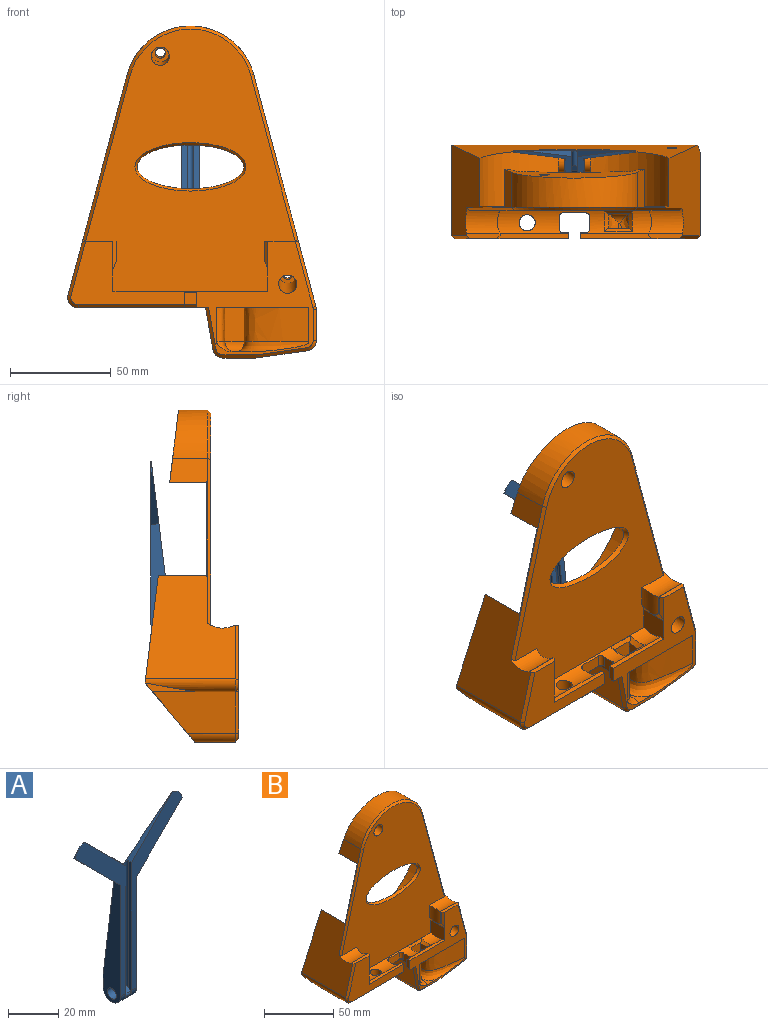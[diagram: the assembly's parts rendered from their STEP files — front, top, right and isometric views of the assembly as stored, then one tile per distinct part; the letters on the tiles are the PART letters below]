
ASSEMBLY  parts=2 mates=1
PART A: 19 faces, bbox 60.4x10x90.5 mm
  f0: plane 85.53x28.64mm, normal (0,-1,0), area 447.3mm2, adj f1,f6,f7,f8,f12,f16
  f1: plane 24.68x24.68mm, normal (0.71,0,0.71), area 51.3mm2, adj f0,f2,f8,f13,f14,f16
  f2: plane 24.68x24.68mm, normal (-0.71,0,0.71), area 51.3mm2, adj f1,f3,f10,f13,f14,f15
  f3: cylinder r=7.37mm len=5.52mm, axis (0,-1,0), area 3.3mm2, adj f2,f4,f10,f13
  f4: plane 25.69x25.69mm, normal (0.71,0,-0.71), area 86.6mm2, adj f3,f5,f10,f13
  f5: plane 59.32x10mm, normal (1,0,0), area 414.2mm2, adj f4,f9,f10,f11,f12,f13
  f6: plane 59.32x10mm, normal (-1,0,0), area 414.2mm2, adj f0,f7,f9,f11,f12,f13
  f7: plane 25.69x25.69mm, normal (-0.71,0,-0.71), area 86.6mm2, adj f0,f6,f8,f13
  f8: cylinder r=7.37mm len=5.52mm, axis (0,-1,0), area 3.3mm2, adj f0,f1,f7,f13
  f9: plane 9x5.12mm, normal (0,1,0), area 46.1mm2, adj f5,f6,f12,f13
  f10: plane 85.53x28.64mm, normal (0,-1,0), area 447.3mm2, adj f2,f3,f4,f5,f12,f15
  f11: cylinder r=2.5mm len=9mm, axis (-1,0,0), area 141.4mm2, adj f5,f6
  f12: cylinder r=5mm len=10mm, axis (1,0,0), area 135.6mm2, adj f0,f5,f6,f9,f10,f15,f16,f18
  f13: plane 80.4x60.39mm, normal (0,0.99,0.12), area 1047.4mm2, adj f1,f2,f3,f4,f5,f6,f7,f8
  f14: cylinder r=1.55mm len=61.93mm, axis (0,0,-1), area 294mm2, adj f1,f2,f15,f16,f17
  f15: plane 64.21x1.55mm, normal (-1,0,0), area 97.3mm2, adj f2,f10,f12,f14,f17,f18
  f16: plane 64.21x1.55mm, normal (1,0,0), area 97.3mm2, adj f0,f1,f12,f14,f17,f18
  f17: plane 3.1x2.47mm, normal (0,-0.71,0.71), area 9.4mm2, adj f14,f15,f16,f18
  f18: cylinder r=1.27mm len=3.1mm, axis (1,0,0), area 4.6mm2, adj f12,f15,f16,f17
PART B: 140 faces, bbox 131x59.5x172.5 mm
  f0: plane 75.23x41.99mm, normal (0,0.99,0.12), area 1163.9mm2, adj f4,f12,f13,f14,f107,f108,f109,f112
  f1: plane 6.24x3mm, normal (0,1,0), area 18.2mm2, adj f6,f116,f118,f123
  f2: plane 6.24x3mm, normal (0,-1,0), area 18.2mm2, adj f6,f116,f118,f123
  f3: plane 6.24x3mm, normal (0,-1,0), area 18.2mm2, adj f6,f115,f119,f124
  f4: cylinder r=48.5mm len=69.3mm, axis (0,1,0), area 1147.9mm2, adj f0,f12,f13,f24,f107,f109,f110,f111
  f5: cylinder r=14.2mm len=77mm, axis (1,0,0), area 556.4mm2, adj f15,f17,f23,f26,f27,f28,f35,f36
  f6: cylinder r=48.5mm len=93.95mm, axis (0,1,0), area 3125mm2, adj f1,f2,f3,f8,f12,f13,f24,f45
  f7: plane 122.25x24.66mm, normal (0,0.17,-0.99), area 1522.5mm2, adj f8,f11,f13,f45,f48,f80,f81,f88
  f8: plane 30.09x22.08mm, normal (-1,0,0), area 307.2mm2, adj f6,f7,f48,f62,f67,f69,f78,f80
  f9: plane 60.37x58.87mm, normal (0,-1,0), area 969.9mm2, adj f10,f22,f26,f27,f43,f50,f51,f52
  f10: plane 6.02x2.13mm, normal (0,0,-1), area 8.3mm2, adj f9,f43,f62,f76,f77,f98
  f11: plane 63.38x20.5mm, normal (0,0,-1), area 904.7mm2, adj f7,f62,f71,f72,f73,f74,f75,f78
  f12: plane 110.42x45.86mm, normal (-0.97,0,0.26), area 2103.6mm2, adj f0,f4,f6,f14,f21,f24,f31,f32
  f13: plane 116.17x46.11mm, normal (0.97,0,0.26), area 2366.1mm2, adj f0,f4,f6,f7,f14,f20,f22,f24
  f14: cylinder r=32.56mm len=62.91mm, axis (0,1,0), area 1488.8mm2, adj f0,f12,f13,f103
  f15: plane 35.5x2.57mm, normal (0,0,1), area 91.2mm2, adj f5,f16,f28,f44
  f16: plane 56.46x31.5mm, normal (0,-1,0), area 787.3mm2, adj f15,f21,f28,f44,f99,f100,f101,f106
  f17: plane 6.32x2.5mm, normal (0,1,0), area 15.8mm2, adj f5,f37,f44,f70
  f18: plane 10x1.07mm, normal (1,0,0), area 10.7mm2, adj f21,f29,f31,f33,f106
  f19: plane 10x1.07mm, normal (-1,0,0), area 10.7mm2, adj f22,f25,f30,f34,f105
  f20: cylinder r=12.7mm len=16.68mm, axis (1,0,0), area 186.9mm2, adj f13,f23,f30,f34,f102
  f21: plane 16.66x2.57mm, normal (0,0,1), area 40.5mm2, adj f12,f16,f18,f31,f99,f106
  f22: plane 16.66x2.57mm, normal (0,0,1), area 40.5mm2, adj f9,f13,f19,f30,f90,f105
  f23: plane 132.71x106.42mm, normal (0,-1,0), area 8567.5mm2, adj f5,f20,f25,f26,f28,f29,f32,f33
  f24: plane 97.01x93.96mm, normal (0,1,0), area 6085.5mm2, adj f4,f6,f12,f13,f82
  f25: plane 21.47x11.59mm, normal (-0.94,0,-0.34), area 27.5mm2, adj f19,f23,f26,f34,f105
  f26: plane 14x12.08mm, normal (-1,0,0), area 161.5mm2, adj f5,f9,f23,f25,f27
  f27: plane 35.5x2.57mm, normal (0,0,1), area 91.2mm2, adj f5,f9,f26,f43
  f28: plane 14x12.08mm, normal (1,0,0), area 161.5mm2, adj f5,f15,f16,f23,f29
  f29: plane 21.47x11.59mm, normal (0.94,0,-0.34), area 27.5mm2, adj f18,f23,f28,f33,f106
  f30: plane 16.68x0.1mm, normal (0,1,0), area 1.7mm2, adj f13,f19,f20,f22
  f31: plane 16.68x0.1mm, normal (0,1,0), area 1.7mm2, adj f12,f18,f21,f32
  f32: cylinder r=12.7mm len=16.68mm, axis (1,0,0), area 186.9mm2, adj f12,f23,f31,f33,f104
  f33: cylinder r=12.7mm len=11.43mm, axis (0,0,1), area 118mm2, adj f18,f23,f29,f32
  f34: cylinder r=12.7mm len=11.43mm, axis (0,0,1), area 118mm2, adj f19,f20,f23,f25
  f35: cylinder r=2mm len=6.32mm, axis (0,0,-1), area 18.9mm2, adj f5,f36,f42,f77
  f36: plane 6.32x2.5mm, normal (0,1,0), area 15.8mm2, adj f5,f35,f43,f76
  f37: cylinder r=2mm len=6.32mm, axis (0,0,-1), area 18.9mm2, adj f5,f17,f38,f71
  f38: plane 6x5.68mm, normal (1,0,0), area 32.4mm2, adj f5,f37,f39,f72
  f39: cylinder r=2mm len=6.1mm, axis (0,0,-1), area 18.3mm2, adj f5,f38,f40,f73
  f40: plane 11x6.1mm, normal (0,-1,0), area 67.2mm2, adj f5,f39,f41,f74
  f41: cylinder r=2mm len=6.1mm, axis (0,0,-1), area 18.3mm2, adj f5,f40,f42,f75
  f42: plane 12.87x8.31mm, normal (-1,0,0), area 46.9mm2, adj f5,f35,f41,f62,f75,f77
  f43: plane 8x3mm, normal (-1,0,0), area 22.8mm2, adj f5,f9,f10,f27,f36,f76
  f44: plane 8x3mm, normal (1,0,0), area 21.7mm2, adj f5,f15,f16,f17,f70,f101
  f45: plane 122.31x53.63mm, normal (0,0.99,0.12), area 3276.3mm2, adj f6,f7,f12,f13,f88,f135
  f46: plane 40.92x15.7mm, normal (1,0,0), area 538.9mm2, adj f48,f86,f89,f92
  f47: plane 20.5x15.97mm, normal (0,0,-1), area 327.5mm2, adj f48,f85,f87,f96
  f48: plane 56.54x30.84mm, normal (0,0.77,-0.64), area 1935.9mm2, adj f7,f8,f13,f46,f47,f62,f66,f85
  f49: plane 23.08x11.09mm, normal (0,-1,0), area 223.7mm2, adj f50,f51,f54,f55,f58,f60,f61,f64
  f50: extruded ~17x12.7mm, area 247.1mm2, adj f9,f49,f53,f57,f65
  f51: extruded ~32.06x17mm, area 639.3mm2, adj f9,f49,f53,f63
  f52: plane 9.43x7.72mm, normal (0,0,1), area 27.1mm2, adj f9,f63,f64,f65
  f53: plane 45.81x12.7mm, normal (0,0,-1), area 139.6mm2, adj f9,f50,f51,f54,f55,f56
  f54: plane 7.7x5.34mm, normal (1,0,0), area 37.7mm2, adj f49,f53,f56,f57,f61
  f55: plane 7.7x5.34mm, normal (-1,0,0), area 37.7mm2, adj f49,f53,f56,f58
  f56: plane 10.79x5.64mm, normal (0,1,0), area 54.8mm2, adj f53,f54,f55,f58,f59,f61
  f57: plane 0.8x0mm, normal (0,0,1), area 0mm2, adj f50,f54
  f58: cone r=16.27mm half-angle=45deg, axis (-1,0,0), area 25.7mm2, adj f5,f49,f55,f56,f59,f60
  f59: plane 13.94x2.08mm, normal (0,0.82,0.58), area 29.6mm2, adj f5,f56,f58,f61
  f60: plane 13.93x2.02mm, normal (0,-0.84,0.55), area 28.3mm2, adj f5,f49,f58,f61
  f61: cone r=14.2mm half-angle=45deg, axis (1,0,0), area 25.7mm2, adj f5,f49,f54,f56,f59,f60
  f62: plane 41.48x20.8mm, normal (-0.98,0,-0.17), area 691.8mm2, adj f8,f10,f11,f42,f48,f87,f98
  f63: bspline ~40.84x18.7mm, area 185.6mm2, adj f9,f51,f52,f64
  f64: cylinder r=5mm len=9.67mm, axis (-1,0,0), area 49.5mm2, adj f49,f52,f63,f65
  f65: bspline ~18.85x9.72mm, area 86.8mm2, adj f9,f50,f52,f64
  f66: plane 25.28x23.52mm, normal (0.14,0,-0.99), area 562.3mm2, adj f48,f85,f86,f94
  f67: plane 20.58x15mm, normal (0,1,0), area 302.9mm2, adj f6,f8,f68,f78
  f68: plane 20.58x12.26mm, normal (1,0,0), area 241.3mm2, adj f6,f67,f69,f79,f80,f81
  f69: plane 18.9x15mm, normal (0,-1,0), area 277.7mm2, adj f6,f8,f68,f80
  f70: plane 2.5x1.5mm, normal (0,0.71,-0.71), area 5.3mm2, adj f17,f44,f71,f101
  f71: cone r=2mm half-angle=45deg, axis (0,0,-1), area 9.2mm2, adj f11,f37,f70,f72
  f72: plane 6x1.5mm, normal (0.71,0,-0.71), area 12.7mm2, adj f11,f38,f71,f73
  f73: cone r=2mm half-angle=45deg, axis (0,0,-1), area 9.2mm2, adj f11,f39,f72,f74
  f74: plane 11x1.5mm, normal (0,-0.71,-0.71), area 23.3mm2, adj f11,f40,f73,f75
  f75: cone r=2mm half-angle=45deg, axis (0,0,-1), area 6.1mm2, adj f11,f41,f42,f74
  f76: plane 2.5x1.5mm, normal (0,0.71,-0.71), area 5.3mm2, adj f10,f36,f43,f77
  f77: cone r=2mm half-angle=45deg, axis (0,0,-1), area 6.1mm2, adj f10,f35,f42,f76
  f78: plane 16.5x1.5mm, normal (0,0.71,-0.71), area 33.4mm2, adj f8,f11,f67,f79
  f79: plane 5.5x1.5mm, normal (0.71,0,-0.71), area 9.9mm2, adj f11,f68,f78,f81
  f80: plane 16.5x1.76mm, normal (0,-0.64,-0.77), area 35.9mm2, adj f7,f8,f68,f69,f81
  f81: plane 9.89x2.97mm, normal (0.71,0.12,-0.7), area 19.5mm2, adj f7,f68,f79,f80
  f82: bspline ~55.19x24.07mm, area 290.8mm2, adj f23,f24
  f83: cylinder r=4mm len=8mm, axis (0,0,-1), area 133.2mm2, adj f5,f84
  f84: cone r=5.5mm half-angle=45deg, axis (0,0,-1), area 63.3mm2, adj f11,f83
  f85: cylinder r=5.08mm len=20.54mm, axis (0,1,0), area 14.6mm2, adj f47,f48,f66,f95
  f86: cylinder r=5.08mm len=27.74mm, axis (0,-1,0), area 186.4mm2, adj f46,f48,f66,f93
  f87: cylinder r=5.08mm len=24.02mm, axis (0,1,0), area 157.9mm2, adj f47,f48,f62,f97
  f88: cylinder r=5.08mm len=45.16mm, axis (0,-1,0), area 305.9mm2, adj f7,f11,f12,f45,f100
  f89: cylinder r=5.08mm len=42.02mm, axis (0,-1,0), area 55.1mm2, adj f13,f46,f48,f91
  f90: plane 32.74x10.22mm, normal (0.68,-0.71,0.18), area 71.5mm2, adj f9,f13,f22,f91
  f91: cone r=3.58mm half-angle=45deg, axis (0,1,0), area 2.4mm2, adj f9,f89,f90,f92
  f92: plane 15.7x1.5mm, normal (0.71,-0.71,0), area 33.3mm2, adj f9,f46,f91,f93
  f93: cone r=3.58mm half-angle=45deg, axis (0,1,0), area 13.1mm2, adj f9,f86,f92,f94
  f94: plane 25.48x5.04mm, normal (0.1,-0.71,-0.7), area 54.1mm2, adj f9,f66,f93,f95
  f95: cone r=3.58mm half-angle=45deg, axis (0,1,0), area 1.3mm2, adj f9,f85,f94,f96
  f96: plane 15.97x1.5mm, normal (0,-0.71,-0.71), area 33.9mm2, adj f9,f47,f95,f97
  f97: cone r=3.58mm half-angle=45deg, axis (0,1,0), area 12.8mm2, adj f9,f87,f96,f98
  f98: plane 20.8x5.15mm, normal (-0.7,-0.71,-0.12), area 44.5mm2, adj f9,f10,f62,f97
  f99: plane 26.99x8.68mm, normal (-0.68,-0.71,0.18), area 58.9mm2, adj f12,f16,f21,f100
  f100: cone r=3.58mm half-angle=45deg, axis (0,1,0), area 16.8mm2, adj f16,f88,f99,f101
  f101: plane 52.88x1.5mm, normal (0,-0.71,-0.71), area 112.2mm2, adj f11,f16,f44,f70,f100
  f102: plane 82.91x23.45mm, normal (0.68,-0.71,0.18), area 180.6mm2, adj f13,f20,f23,f103
  f103: cone r=32.56mm half-angle=45deg, axis (0,1,0), area 176.7mm2, adj f14,f23,f102,f104
  f104: plane 82.91x23.45mm, normal (-0.68,-0.71,0.18), area 180.6mm2, adj f12,f23,f32,f103
  f105: plane 14.12x1.5mm, normal (-0.71,-0.71,0), area 25.6mm2, adj f9,f19,f22,f25
  f106: plane 14.12x1.5mm, normal (0.71,-0.71,0), area 25.6mm2, adj f16,f18,f21,f29
  f107: plane 1.38x0.73mm, normal (-0.71,0,0.71), area 1.4mm2, adj f0,f4,f108,f110
  f108: cylinder r=7.62mm len=5.66mm, axis (0,-1,0), area 8mm2, adj f0,f107,f109,f110
  f109: plane 1.94x1.94mm, normal (0.71,0,-0.71), area 2mm2, adj f0,f4,f108,f110
  f110: plane 7.6x6.39mm, normal (0,1,0), area 20.3mm2, adj f4,f107,f108,f109
  f111: plane 7.6x6.39mm, normal (0,1,0), area 20.3mm2, adj f4,f112,f113,f114
  f112: plane 1.38x0.73mm, normal (0.71,0,0.71), area 1.4mm2, adj f0,f4,f111,f114
  f113: plane 1.94x1.94mm, normal (-0.71,0,-0.71), area 2mm2, adj f0,f4,f111,f114
  f114: cylinder r=7.62mm len=5.66mm, axis (0,-1,0), area 8mm2, adj f0,f111,f112,f113
  f115: plane 10.84x10mm, normal (-1,0,0), area 97.6mm2, adj f3,f6,f117,f124
  f116: plane 10.84x10mm, normal (1,0,0), area 97.6mm2, adj f1,f2,f6,f123
  f117: plane 6.24x3mm, normal (0,1,0), area 18.2mm2, adj f6,f115,f119,f124
  f118: plane 11.24x10mm, normal (-1,0,0), area 80.1mm2, adj f1,f2,f6,f120,f121,f122,f123,f125
  f119: plane 11.24x10mm, normal (1,0,0), area 80.1mm2, adj f3,f6,f117,f120,f121,f122,f124,f125
  f120: plane 10x6mm, normal (0,0,1), area 60mm2, adj f118,f119,f121,f122
  f121: plane 10.52x2.02mm, normal (0,-0.71,0.71), area 20mm2, adj f6,f118,f119,f120
  f122: plane 10.52x2.02mm, normal (0,0.71,0.71), area 20mm2, adj f6,f118,f119,f120
  f123: cylinder r=5mm len=10mm, axis (-1,0,0), area 47.1mm2, adj f1,f2,f116,f118
  f124: cylinder r=5mm len=10mm, axis (-1,0,0), area 47.1mm2, adj f3,f115,f117,f119
  f125: cylinder r=2mm len=10mm, axis (1,0,0), area 125.7mm2, adj f118,f119
  f126: plane 17.47x15mm, normal (0,1,0), area 253.1mm2, adj f4,f127,f129,f130,f132,f133
  f127: plane 14.93x11mm, normal (-1,0,0), area 163.4mm2, adj f4,f126,f128,f131,f132
  f128: plane 15x13.66mm, normal (0,-1,0), area 198.7mm2, adj f4,f127,f129,f131
  f129: plane 14.88x11mm, normal (1,0,0), area 162.9mm2, adj f4,f126,f128,f131,f133
  f130: plane 9.92x7.19mm, normal (0,0,-1), area 71.3mm2, adj f126,f131,f132,f133
  f131: plane 16.07x4.88mm, normal (0,-0.71,-0.71), area 76.9mm2, adj f127,f128,f129,f130,f132,f133
  f132: cylinder r=2.54mm len=9.73mm, axis (0,1,0), area 33.8mm2, adj f126,f127,f130,f131
  f133: cylinder r=2.54mm len=9.73mm, axis (0,-1,0), area 33.8mm2, adj f126,f129,f130,f131
  f134: cylinder r=2.5mm len=5.57mm, axis (0,0.99,0.12), area 78.5mm2, adj f0,f138
  f135: cylinder r=2.5mm len=5.57mm, axis (0,0.99,0.12), area 78.5mm2, adj f45,f136
  f136: plane 9x8.93mm, normal (0,-0.99,-0.12), area 44mm2, adj f135,f137
  f137: cylinder r=4.5mm len=40.66mm, axis (0,0.99,0.12), area 1127.1mm2, adj f9,f136
  f138: plane 9x8.93mm, normal (0,-0.99,-0.12), area 44mm2, adj f134,f139
  f139: cylinder r=4.5mm len=13.17mm, axis (0,0.99,0.12), area 343.9mm2, adj f23,f138
PLACE A rot(axis=(-1,0,0),7deg) t=(31.88,-27.51,-8.02)mm
PLACE B t=(31.87,-24.21,-10.18)mm
MATE cylindrical A.f11 <-> B.f123  axis (1,0,0) through (36.38,-8.21,17.82)mm
